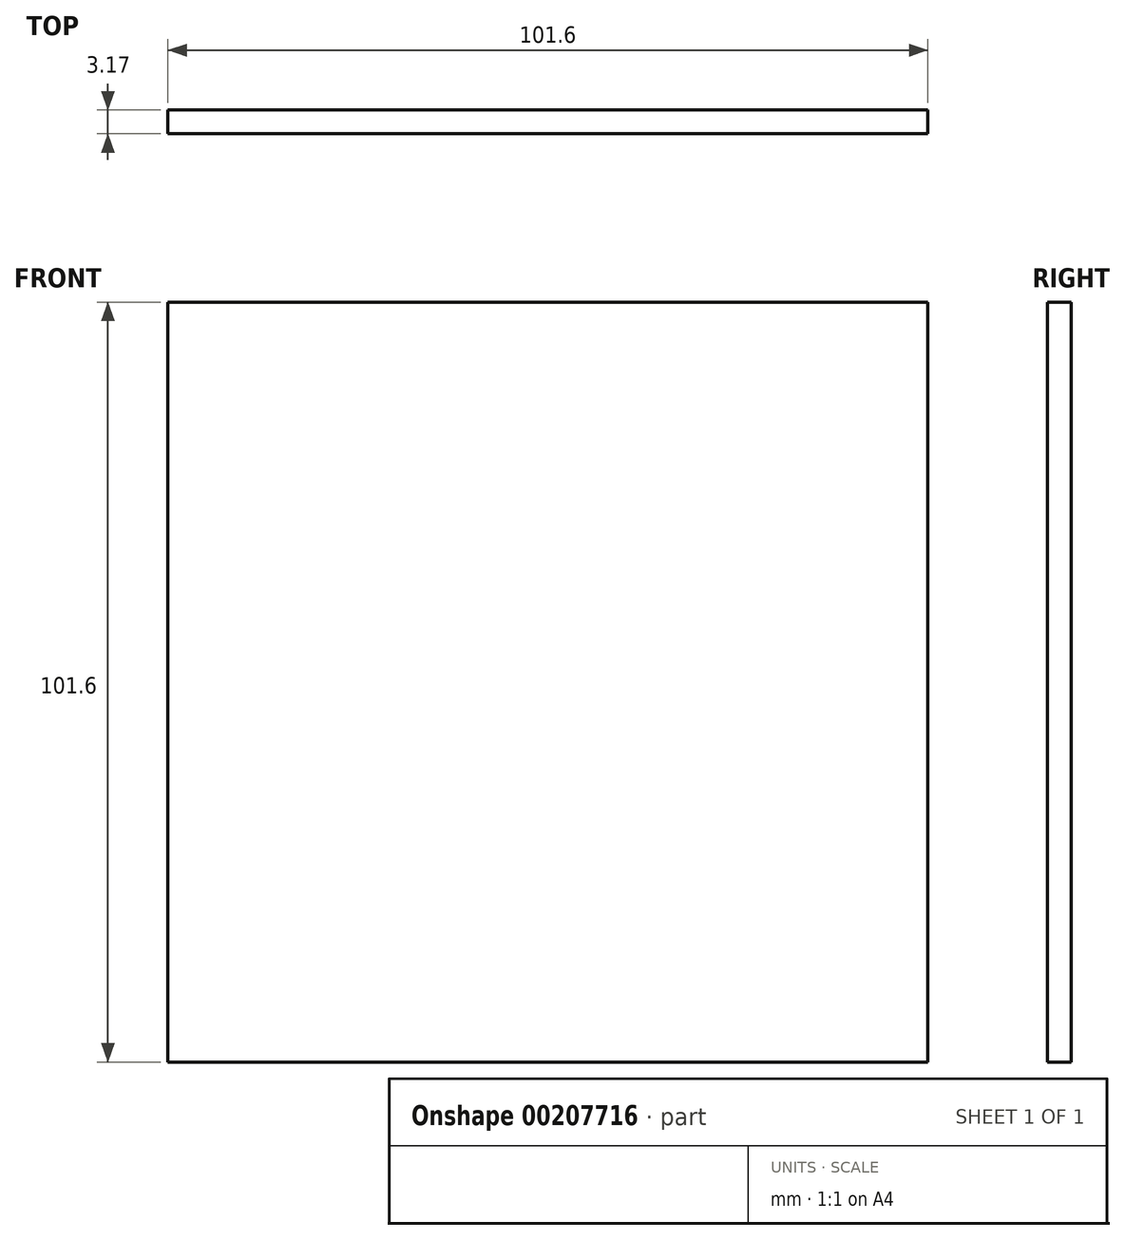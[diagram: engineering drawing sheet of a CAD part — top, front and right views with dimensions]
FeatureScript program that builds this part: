
annotation { "Feature Type Name" : "Feature", "Feature Type Description" : "" }
export const myFeature = defineFeature(function(context is Context, id is Id, definition is map)
    precondition{}
    {
        {
            var Q0;
            Q0=qCreatedBy(makeId("Front.planeOp"),FACE);
            var sketch = newSketch(context, id + "F0", { "sketchPlane" : qUnion([Q0])});
            skLineSegment(sketch, "E0.bottom", {"start": v(0, -50.8) * mm, "end": v(101.6, -50.8) * mm});
            skLineSegment(sketch, "E0.top", {"start": v(0, 50.8) * mm, "end": v(101.6, 50.8) * mm});
            skLineSegment(sketch, "E0.left", {"start": v(0, -50.8) * mm, "end": v(0, 50.8) * mm});
            skLineSegment(sketch, "E0.right", {"start": v(101.6, -50.8) * mm, "end": v(101.6, 50.8) * mm});
            skSolve(sketch);
        }
        {
            var Q0;
            Q0 = qSketchRegion(id + "F0", true);
            extrude(context, id + "F1", {"entities" : qUnion([Q0]), "depth" : 3.17 * mm});
        }
    });
